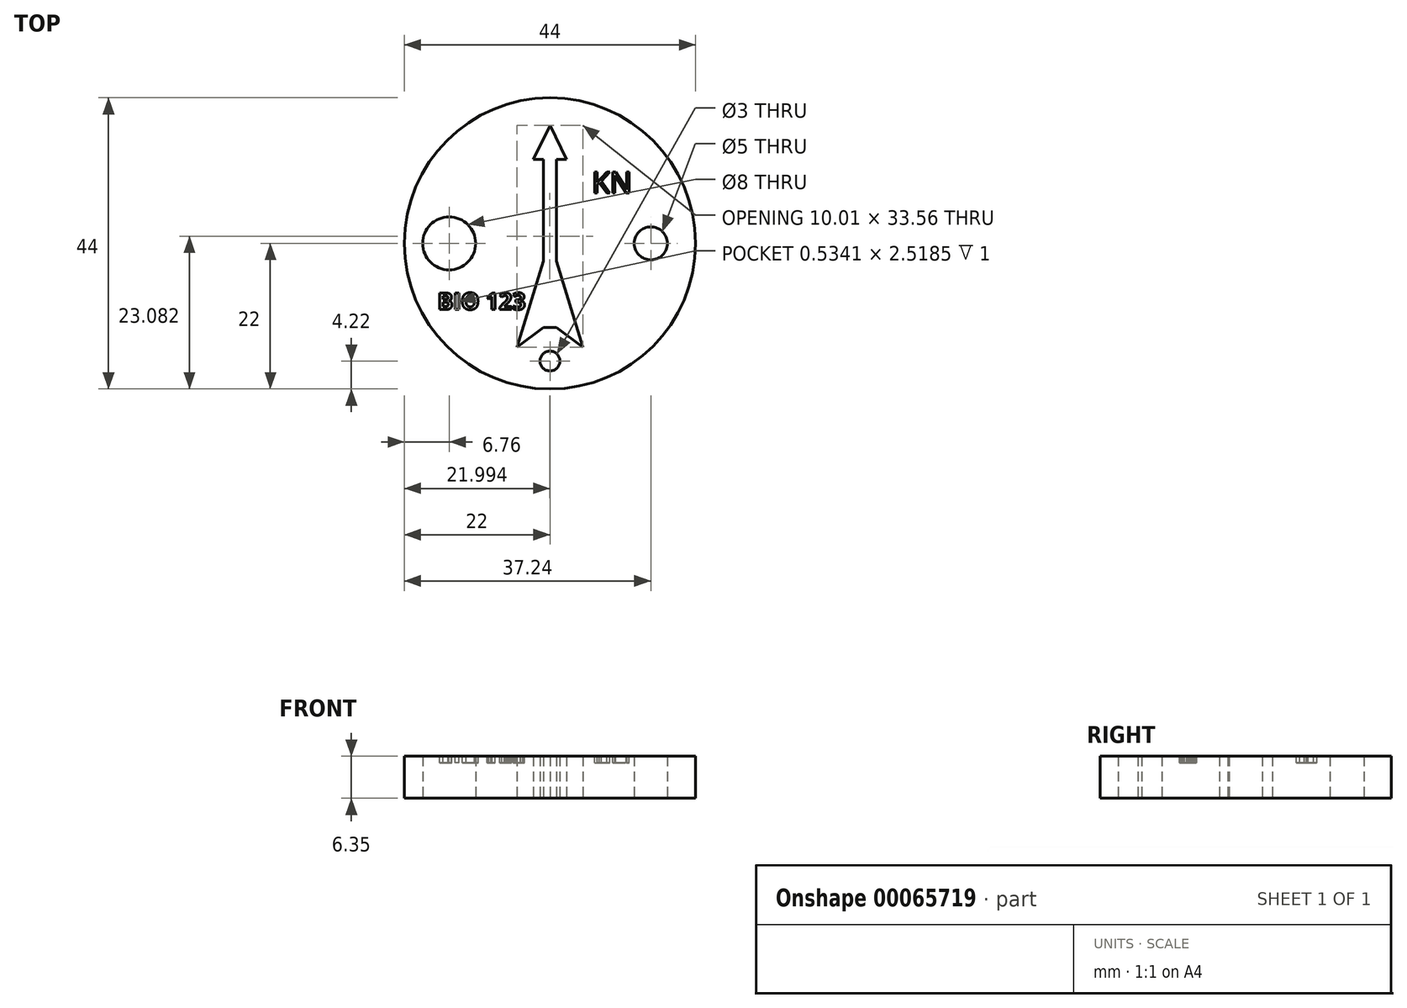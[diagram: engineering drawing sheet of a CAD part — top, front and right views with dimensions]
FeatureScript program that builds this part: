
annotation { "Feature Type Name" : "Feature", "Feature Type Description" : "" }
export const myFeature = defineFeature(function(context is Context, id is Id, definition is map)
    precondition{}
    {
        {
            var Q0;
            Q0=qCreatedBy(makeId("Top.planeOp"),FACE);
            var sketch = newSketch(context, id + "F0", { "sketchPlane" : qUnion([Q0])});
            skLineSegment(sketch, "E0.rect.bottom", {"start": v(1, 12.7) * mm, "end": v(-1, 12.7) * mm});
            skLineSegment(sketch, "E0.rect.top", {"start": v(1, -12.7) * mm, "end": v(-1, -12.7) * mm});
            skLineSegment(sketch, "E0.rect.left", {"start": v(1, 12.7) * mm, "end": v(1, -12.7) * mm});
            skLineSegment(sketch, "E0.rect.right", {"start": v(-1, 12.7) * mm, "end": v(-1, -12.7) * mm});
            skPoint(sketch, "E0.rect.middle", {"position": v(0, 0) * mm});
            skLineSegment(sketch, "E1", {"start": v(-1, 12.7) * mm, "end": v(-2.5, 12.7) * mm});
            skLineSegment(sketch, "E2", {"start": v(-2.5, 12.7) * mm, "end": v(0, 17.86) * mm});
            skLineSegment(sketch, "E3", {"start": v(0, 17.86) * mm, "end": v(2.5, 12.7) * mm});
            skLineSegment(sketch, "E4", {"start": v(2.5, 12.7) * mm, "end": v(1, 12.7) * mm});
            skLineSegment(sketch, "E5", {"start": v(-2.5, 12.7) * mm, "end": v(9.08, 12.7) * mm, "construction": true});
            skLineSegment(sketch, "E6", {"start": v(-1, -2.7) * mm, "end": v(-5.01, -15.7) * mm});
            skLineSegment(sketch, "E7", {"start": v(-5.01, -15.7) * mm, "end": v(-1, -12.7) * mm});
            skLineSegment(sketch, "E8", {"start": v(1, -2.7) * mm, "end": v(5, -15.7) * mm});
            skLineSegment(sketch, "E9", {"start": v(5, -15.7) * mm, "end": v(1, -12.7) * mm});
            skLineSegment(sketch, "E10", {"start": v(1, -2.7) * mm, "end": v(-6.77, -2.7) * mm, "construction": true});
            skLineSegment(sketch, "E11", {"start": v(5, -15.7) * mm, "end": v(-9.76, -15.7) * mm, "construction": true});
            skCircle(sketch, "E12", {"center": v(-15.24, 0) * mm, "radius": 4 * mm});
            skCircle(sketch, "E13", {"center": v(15.24, 0) * mm, "radius": 2.5 * mm});
            skCircle(sketch, "E14", {"center": v(0, -17.78) * mm, "radius": 1.5 * mm});
            skLineSegment(sketch, "E15", {"start": v(-22.69, 0) * mm, "end": v(22.45, 0) * mm, "construction": true});
            skLineSegment(sketch, "E16", {"start": v(0, -16.52) * mm, "end": v(0, -18.97) * mm, "construction": true});
            skCircle(sketch, "E17", {"center": v(0, 0) * mm, "radius": 22 * mm});
            skSolve(sketch);
        }
        {
            var Q0;
            Q0=makeQuery(id+"F0.imprint","IMPRINT",FACE,{"disambiguationData":[TD([[makeQuery(id+"F0.imprint","IMPRINT",EDGE,{"derivedFrom":sQuery(id+"F0.wireOp",EDGE,"E0.rect.top")}),1.0]])]});
            extrude(context, id + "F1", {"entities" : qUnion([Q0]), "depth" : 6.35 * mm});
        }
        {
            var Q0;
            Q0=makeQuery(id+"F1.opExtrude","CAP_FACE",FACE,{"disambiguationData":[OSD([sQuery(id+"F0.wireOp",EDGE,"E0.rect.top"),sQuery(id+"F0.wireOp",EDGE,"E0.rect.left"),sQuery(id+"F0.wireOp",EDGE,"E0.rect.right"),sQuery(id+"F0.wireOp",EDGE,"E1"),sQuery(id+"F0.wireOp",EDGE,"E2"),sQuery(id+"F0.wireOp",EDGE,"E3"),sQuery(id+"F0.wireOp",EDGE,"E4"),sQuery(id+"F0.wireOp",EDGE,"E6"),sQuery(id+"F0.wireOp",EDGE,"E7"),sQuery(id+"F0.wireOp",EDGE,"E8"),sQuery(id+"F0.wireOp",EDGE,"E9"),sQuery(id+"F0.wireOp",EDGE,"E12"),sQuery(id+"F0.wireOp",EDGE,"E13"),sQuery(id+"F0.wireOp",EDGE,"E14"),sQuery(id+"F0.wireOp",EDGE,"E17")])],"isStart":false});
            var sketch = newSketch(context, id + "F2", { "sketchPlane" : qUnion([Q0])});
            skText(sketch, "E18", { "text": "BIO 123", "fontName": "OpenSans-Bold.ttf"});
            skText(sketch, "E19", { "text": "KN", "fontName": "OpenSans-Regular.ttf"});
            const initialGuessF2  = {"E18": [-0.017, -0.01, 1, 0, 0.00254], "E19": [0.00635, 0.00762, 1, 0, 0.00318]};
            skSetInitialGuess(sketch, initialGuessF2);
            skSolve(sketch);
        }
        {
            var Q0;
            Q0 = qSketchRegion(id + "F2", true);
            extrude(context, id + "F3", {"entities" : qUnion([Q0]), "operationType" : NewBodyOperationType.REMOVE, "oppositeDirection" : true, "depth" : 1 * mm});
        }
    });
